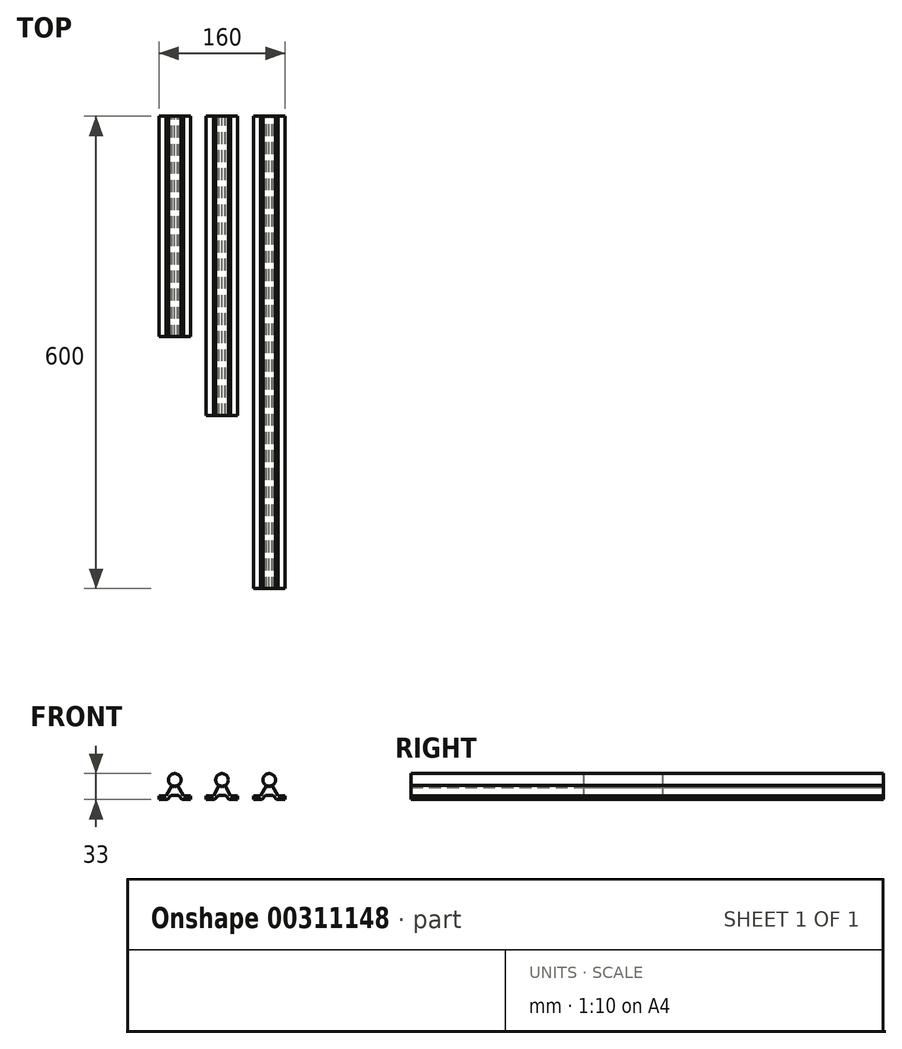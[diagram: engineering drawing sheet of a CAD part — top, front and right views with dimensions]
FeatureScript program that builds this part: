
annotation { "Feature Type Name" : "Feature", "Feature Type Description" : "" }
export const myFeature = defineFeature(function(context is Context, id is Id, definition is map)
    precondition{}
    {
        {
            var Q0;
            Q0=qCreatedBy(makeId("Front.planeOp"),FACE);
            var sketch = newSketch(context, id + "F0", { "sketchPlane" : qUnion([Q0])});
            skCircle(sketch, "E0", {"center": v(0, 0) * mm, "radius": 8 * mm});
            skLineSegment(sketch, "E1", {"start": v(20, -25) * mm, "end": v(20, -20) * mm});
            skLineSegment(sketch, "E2", {"start": v(20, -20) * mm, "end": v(11, -20) * mm});
            skLineSegment(sketch, "E3", {"start": v(11, -20) * mm, "end": v(3.6, -7.2) * mm});
            skLineSegment(sketch, "E4", {"start": v(3.6, -7.2) * mm, "end": v(0, -9.28) * mm});
            skLineSegment(sketch, "E5", {"start": v(0, -9.28) * mm, "end": v(-3.6, -7.2) * mm});
            skLineSegment(sketch, "E6", {"start": v(-3.6, -7.2) * mm, "end": v(-11, -20) * mm});
            skLineSegment(sketch, "E7", {"start": v(-11, -20) * mm, "end": v(-20, -20) * mm});
            skLineSegment(sketch, "E8", {"start": v(-20, -20) * mm, "end": v(-20, -25) * mm});
            skLineSegment(sketch, "E9", {"start": v(-20, -25) * mm, "end": v(-9.25, -25) * mm});
            skLineSegment(sketch, "E10", {"start": v(20, -25) * mm, "end": v(9.25, -25) * mm});
            skLineSegment(sketch, "E11", {"start": v(-9.25, -25) * mm, "end": v(-4.55, -19.4) * mm});
            skLineSegment(sketch, "E12", {"start": v(-4.55, -19.4) * mm, "end": v(4.55, -19.4) * mm});
            skLineSegment(sketch, "E13", {"start": v(9.25, -25) * mm, "end": v(4.55, -19.4) * mm});
            skCircle(sketch, "E14", {"center": v(60, 0) * mm, "radius": 8 * mm});
            skLineSegment(sketch, "E15", {"start": v(80, -25) * mm, "end": v(80, -20) * mm});
            skLineSegment(sketch, "E16", {"start": v(80, -20) * mm, "end": v(71, -20) * mm});
            skLineSegment(sketch, "E17", {"start": v(71, -20) * mm, "end": v(63.6, -7.2) * mm});
            skLineSegment(sketch, "E18", {"start": v(63.6, -7.2) * mm, "end": v(60, -9.28) * mm});
            skLineSegment(sketch, "E19", {"start": v(60, -9.28) * mm, "end": v(56.4, -7.2) * mm});
            skLineSegment(sketch, "E20", {"start": v(56.4, -7.2) * mm, "end": v(49, -20) * mm});
            skLineSegment(sketch, "E21", {"start": v(49, -20) * mm, "end": v(40, -20) * mm});
            skLineSegment(sketch, "E22", {"start": v(40, -20) * mm, "end": v(40, -25) * mm});
            skLineSegment(sketch, "E23", {"start": v(40, -25) * mm, "end": v(50.75, -25) * mm});
            skLineSegment(sketch, "E24", {"start": v(80, -25) * mm, "end": v(69.25, -25) * mm});
            skLineSegment(sketch, "E25", {"start": v(50.75, -25) * mm, "end": v(55.45, -19.4) * mm});
            skLineSegment(sketch, "E26", {"start": v(55.45, -19.4) * mm, "end": v(64.55, -19.4) * mm});
            skLineSegment(sketch, "E27", {"start": v(69.25, -25) * mm, "end": v(64.55, -19.4) * mm});
            skCircle(sketch, "E28", {"center": v(-60, 0) * mm, "radius": 8 * mm});
            skLineSegment(sketch, "E29", {"start": v(-40, -25) * mm, "end": v(-40, -20) * mm});
            skLineSegment(sketch, "E30", {"start": v(-40, -20) * mm, "end": v(-49, -20) * mm});
            skLineSegment(sketch, "E31", {"start": v(-49, -20) * mm, "end": v(-56.4, -7.2) * mm});
            skLineSegment(sketch, "E32", {"start": v(-56.4, -7.2) * mm, "end": v(-60, -9.28) * mm});
            skLineSegment(sketch, "E33", {"start": v(-60, -9.28) * mm, "end": v(-63.6, -7.2) * mm});
            skLineSegment(sketch, "E34", {"start": v(-63.6, -7.2) * mm, "end": v(-71, -20) * mm});
            skLineSegment(sketch, "E35", {"start": v(-71, -20) * mm, "end": v(-80, -20) * mm});
            skLineSegment(sketch, "E36", {"start": v(-80, -20) * mm, "end": v(-80, -25) * mm});
            skLineSegment(sketch, "E37", {"start": v(-80, -25) * mm, "end": v(-69.25, -25) * mm});
            skLineSegment(sketch, "E38", {"start": v(-40, -25) * mm, "end": v(-50.75, -25) * mm});
            skLineSegment(sketch, "E39", {"start": v(-69.25, -25) * mm, "end": v(-64.55, -19.4) * mm});
            skLineSegment(sketch, "E40", {"start": v(-64.55, -19.4) * mm, "end": v(-55.45, -19.4) * mm});
            skLineSegment(sketch, "E41", {"start": v(-50.75, -25) * mm, "end": v(-55.45, -19.4) * mm});
            skSolve(sketch);
        }
        {
            var Q0;
            Q0=makeQuery(id+"F0.imprint","IMPRINT",FACE,{"disambiguationData":[TD([[makeQuery(id+"F0.imprint","IMPRINT",EDGE,{"derivedFrom":sQuery(id+"F0.wireOp",EDGE,"E0")}),1.0]])]});
            var Q1;
            Q1=makeQuery(id+"F0.imprint","IMPRINT",FACE,{"disambiguationData":[TD([[makeQuery(id+"F0.imprint","IMPRINT",EDGE,{"derivedFrom":sQuery(id+"F0.wireOp",EDGE,"E1")}),1.0]])]});
            extrude(context, id + "F1", {"entities" : qUnion([Q0, Q1]), "depth" : 380 * mm});
        }
        {
            var Q0;
            Q0=makeQuery(id+"F0.imprint","IMPRINT",FACE,{"disambiguationData":[TD([[makeQuery(id+"F0.imprint","IMPRINT",EDGE,{"derivedFrom":sQuery(id+"F0.wireOp",EDGE,"E14")}),1.0]])]});
            var Q1;
            Q1=makeQuery(id+"F0.imprint","IMPRINT",FACE,{"disambiguationData":[TD([[makeQuery(id+"F0.imprint","IMPRINT",EDGE,{"derivedFrom":sQuery(id+"F0.wireOp",EDGE,"E15")}),1.0]])]});
            extrude(context, id + "F2", {"entities" : qUnion([Q0, Q1]), "depth" : 600 * mm});
        }
        {
            var Q0;
            Q0=makeQuery(id+"F0.imprint","IMPRINT",FACE,{"disambiguationData":[TD([[makeQuery(id+"F0.imprint","IMPRINT",EDGE,{"derivedFrom":sQuery(id+"F0.wireOp",EDGE,"E28")}),1.0]])]});
            var Q1;
            Q1=makeQuery(id+"F0.imprint","IMPRINT",FACE,{"disambiguationData":[TD([[makeQuery(id+"F0.imprint","IMPRINT",EDGE,{"derivedFrom":sQuery(id+"F0.wireOp",EDGE,"E29")}),1.0]])]});
            extrude(context, id + "F3", {"entities" : qUnion([Q0, Q1]), "depth" : 280 * mm});
        }
    });
